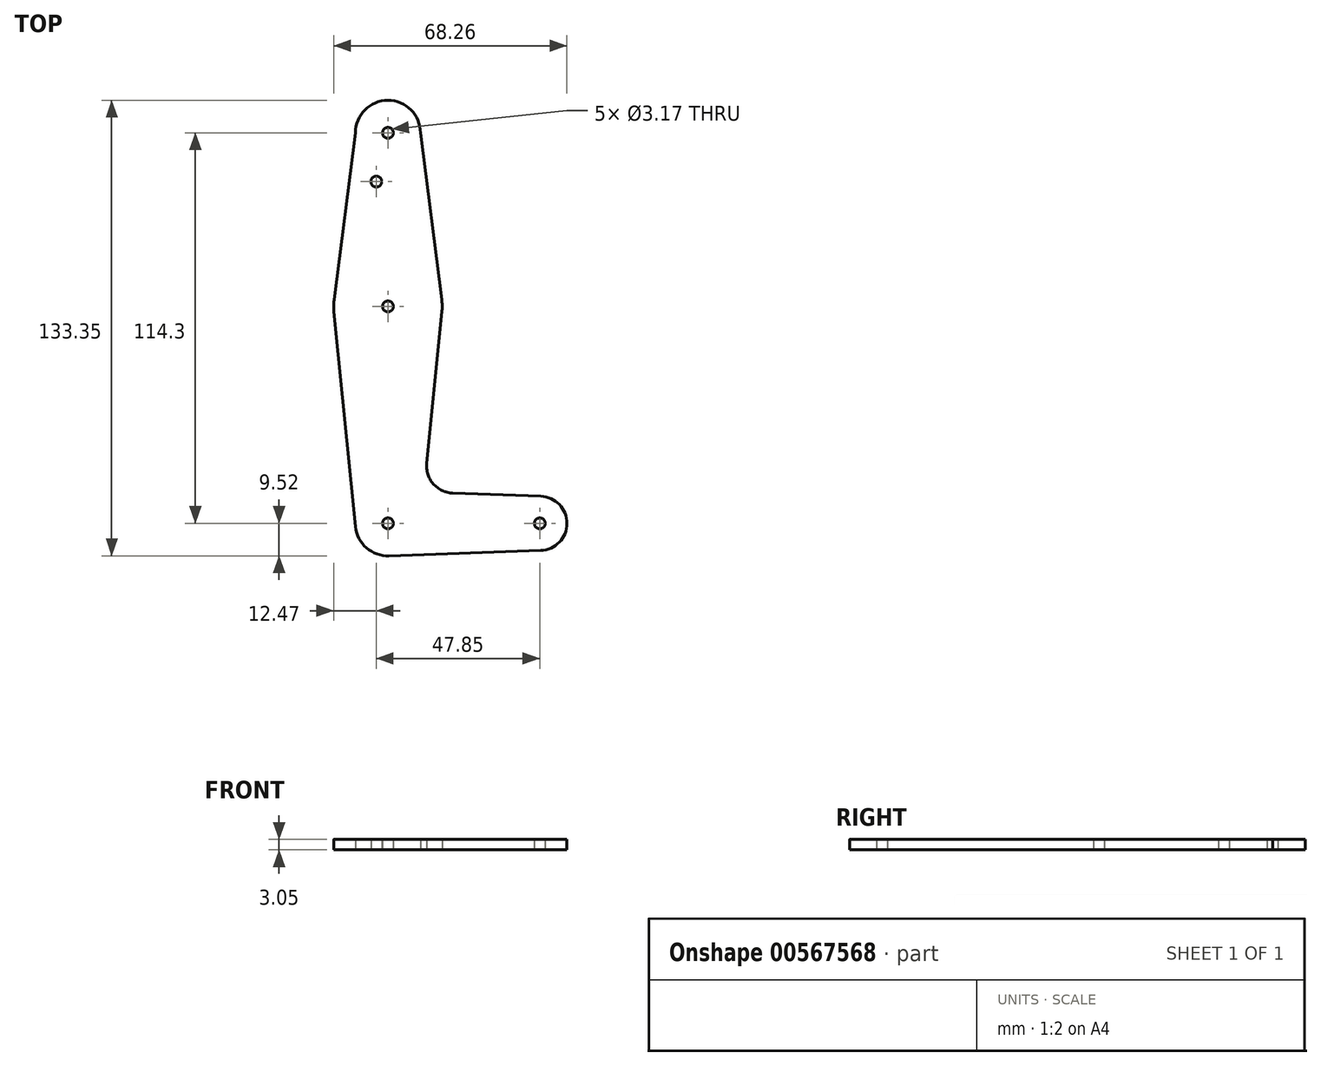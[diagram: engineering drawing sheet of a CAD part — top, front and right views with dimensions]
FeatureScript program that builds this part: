
annotation { "Feature Type Name" : "Feature", "Feature Type Description" : "" }
export const myFeature = defineFeature(function(context is Context, id is Id, definition is map)
    precondition{}
    {
        {
            var Q0;
            Q0=qCreatedBy(makeId("Top.planeOp"),FACE);
            var sketch = newSketch(context, id + "F0", { "sketchPlane" : qUnion([Q0])});
            skLineSegment(sketch, "E0", {"start": v(0, 0) * mm, "end": v(0, 63.5) * mm});
            skLineSegment(sketch, "E1", {"start": v(0, 63.5) * mm, "end": v(0, 114.3) * mm});
            skLineSegment(sketch, "E2", {"start": v(0, 0) * mm, "end": v(44.45, 0) * mm});
            skCircle(sketch, "E3", {"center": v(0, 0) * mm, "radius": 9.53 * mm});
            skCircle(sketch, "E4", {"center": v(0, 63.5) * mm, "radius": 15.88 * mm});
            skCircle(sketch, "E5", {"center": v(0, 114.3) * mm, "radius": 9.53 * mm});
            skCircle(sketch, "E6", {"center": v(44.45, 0) * mm, "radius": 7.94 * mm});
            skLineSegment(sketch, "E7", {"start": v(-9.53, 114.3) * mm, "end": v(-15.75, 65.5) * mm});
            skLineSegment(sketch, "E8", {"start": v(44.73, -7.93) * mm, "end": v(44.73, 7.93) * mm});
            skLineSegment(sketch, "E9", {"start": v(9.53, 114.3) * mm, "end": v(15.75, 65.5) * mm});
            skCircle(sketch, "E10", {"center": v(0, 114.3) * mm, "radius": 1.59 * mm});
            skCircle(sketch, "E11", {"center": v(0, 63.5) * mm, "radius": 1.59 * mm});
            skCircle(sketch, "E12", {"center": v(44.45, 0) * mm, "radius": 1.59 * mm});
            skCircle(sketch, "E13", {"center": v(0, 0) * mm, "radius": 1.59 * mm});
            skCircle(sketch, "E14", {"center": v(-3.4, 100.03) * mm, "radius": 1.59 * mm});
            skLineSegment(sketch, "E15", {"start": v(-15.8, 61.91) * mm, "end": v(-9.48, -0.95) * mm});
            skLineSegment(sketch, "E16", {"start": v(15.8, 61.91) * mm, "end": v(11.34, 17.6) * mm});
            skLineSegment(sketch, "E17", {"start": v(18.97, 8.85) * mm, "end": v(44.73, 7.93) * mm});
            skLineSegment(sketch, "E18", {"start": v(0.34, -9.52) * mm, "end": v(44.73, -7.93) * mm});
            skPoint(sketch, "E19.newPointB", {"position": v(0.34, 9.52) * mm});
            skArc(sketch, "E19.filletArc", {"start": v(11.34, 17.6) * mm, "mid": v(13.26, 11.57) * mm, "end": v(18.97, 8.85) * mm});
            skSolve(sketch);
        }
        {
            var Q0;
            Q0 = qSketchRegion(id + "F0", true);
            var Q1;
            {var subQ0=sQuery(id+"F0.wireOp",EDGE,"E13");var subQ1=sQuery(id+"F0.wireOp",EDGE,"E0");var subQ2=makeQuery(id+"F0.imprint","INTERSECT",VERTEX,{"derivedFrom":[subQ1,subQ0]});Q1=makeQuery(id+"F0.imprint","IMPRINT",FACE,{"disambiguationData":[TD([[makeQuery(id+"F0.imprint","IMPRINT",EDGE,{"disambiguationData":[TD([[subQ2,-1.0]])],"derivedFrom":subQ1}),-1.0]])]});}
            extrude(context, id + "F1", {"entities" : qUnion([Q0, Q1]), "depth" : 3.05 * mm, "offsetDistance" : 25.4 * mm});
        }
    });
